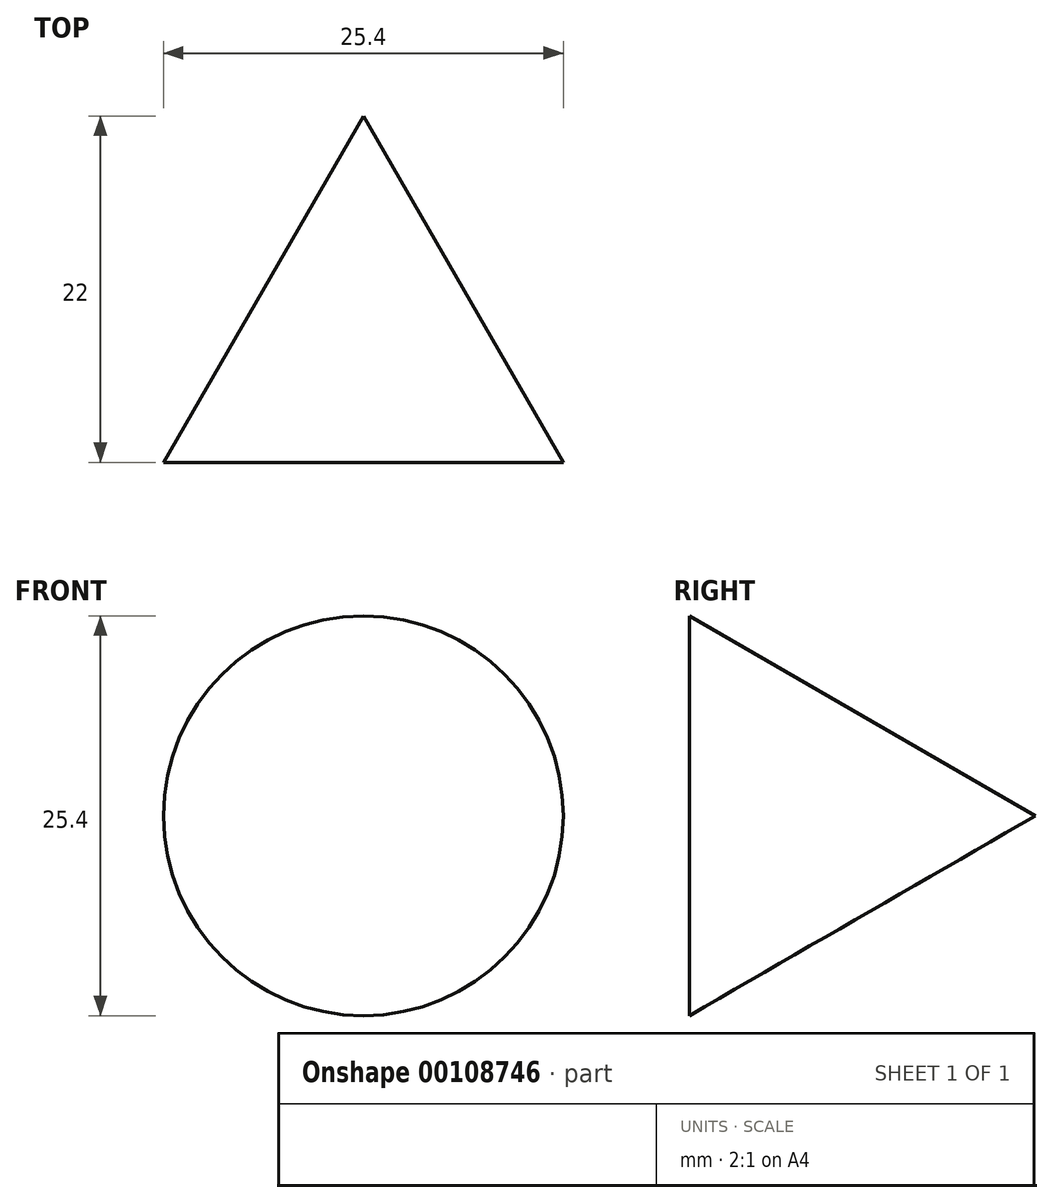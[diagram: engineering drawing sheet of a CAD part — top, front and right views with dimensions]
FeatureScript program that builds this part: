
annotation { "Feature Type Name" : "Feature", "Feature Type Description" : "" }
export const myFeature = defineFeature(function(context is Context, id is Id, definition is map)
    precondition{}
    {
        {
            var Q0;
            Q0=qCreatedBy(makeId("Top.planeOp"),FACE);
            var sketch = newSketch(context, id + "F0", { "sketchPlane" : qUnion([Q0])});
            skLineSegment(sketch, "E0", {"start": v(0, 22) * mm, "end": v(-12.7, 0) * mm});
            skLineSegment(sketch, "E1", {"start": v(-12.7, 0) * mm, "end": v(0, 0) * mm});
            skLineSegment(sketch, "E2", {"start": v(0, 22) * mm, "end": v(0, 0) * mm});
            skSolve(sketch);
        }
        {
            var Q0;
            Q0 = qSketchRegion(id + "F0", true);
            var Q1;
            Q1=sQuery(id+"F0.wireOp",EDGE,"E2");
            revolve(context, id + "F1", {"entities" : qUnion([Q0]), "axis" : qUnion([Q1]), "revolveType" : RevolveType.FULL});
        }
        {
            var Q0;
            Q0=makeQuery(id+"F0.imprint","IMPRINT",FACE,{"disambiguationData":[TD([[makeQuery(id+"F0.imprint","IMPRINT",EDGE,{"derivedFrom":sQuery(id+"F0.wireOp",EDGE,"E0")}),1.0]])]});
            var Q1;
            Q1=sQuery(id+"F0.wireOp",EDGE,"E2");
            revolve(context, id + "F2", {"entities" : qUnion([Q0]), "axis" : qUnion([Q1]), "revolveType" : RevolveType.FULL});
        }
    });
